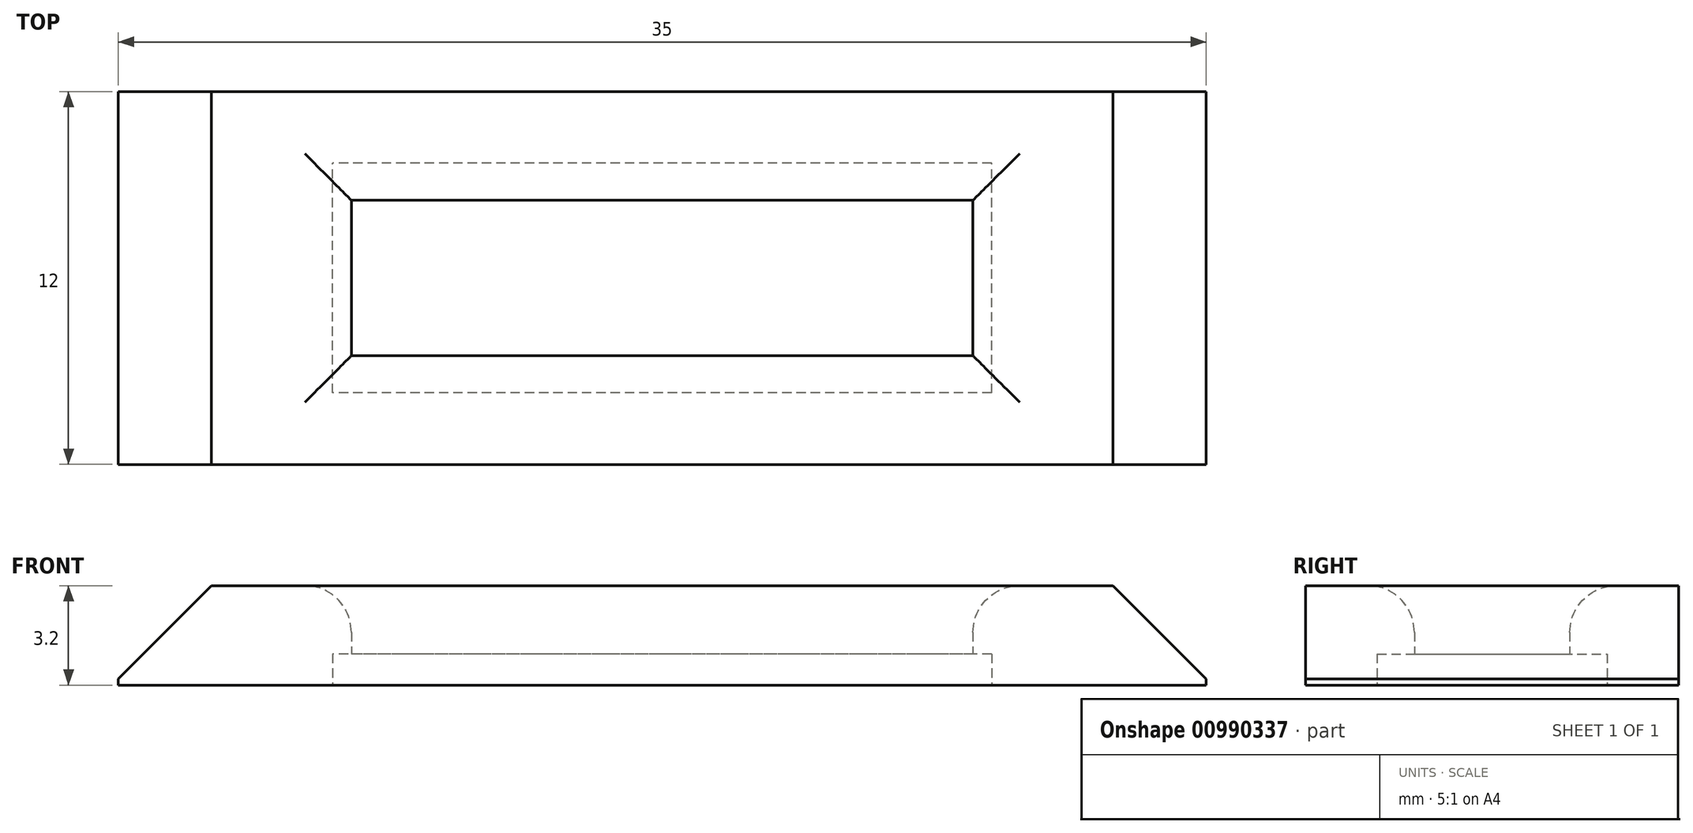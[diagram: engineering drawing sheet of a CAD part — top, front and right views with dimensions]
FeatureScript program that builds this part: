
annotation { "Feature Type Name" : "Feature", "Feature Type Description" : "" }
export const myFeature = defineFeature(function(context is Context, id is Id, definition is map)
    precondition{}
    {
        {
            var Q0;
            Q0=qCreatedBy(makeId("Top.planeOp"),FACE);
            var sketch = newSketch(context, id + "F0", { "sketchPlane" : qUnion([Q0])});
            skLineSegment(sketch, "E0.bottom", {"start": v(-51.31, 31.06) * mm, "end": v(-31.31, 31.06) * mm});
            skLineSegment(sketch, "E0.left", {"start": v(-51.31, 31.06) * mm, "end": v(-51.31, 26.06) * mm});
            skLineSegment(sketch, "E0.right", {"start": v(-31.31, 31.06) * mm, "end": v(-31.31, 26.06) * mm});
            skLineSegment(sketch, "E1.bottom", {"start": v(-58.81, 34.56) * mm, "end": v(-23.81, 34.56) * mm});
            skLineSegment(sketch, "E1.left", {"start": v(-58.81, 34.56) * mm, "end": v(-58.81, 22.56) * mm});
            skLineSegment(sketch, "E1.right", {"start": v(-23.81, 34.56) * mm, "end": v(-23.81, 22.56) * mm});
            skPoint(sketch, "E1.middle", {"position": v(-41.31, 28.56) * mm});
            skPoint(sketch, "E1.middle.positionSnap0", {"position": v(-51.31, 28.56) * mm});
            skPoint(sketch, "E1.middle.positionSnap1", {"position": v(-41.31, 31.06) * mm});
            skPoint(sketch, "E1.centerSnap0", {"position": v(-51.31, 28.56) * mm});
            skPoint(sketch, "E1.centerSnap1", {"position": v(-41.31, 31.06) * mm});
            skLineSegment(sketch, "E2", {"start": v(-58.81, 22.56) * mm, "end": v(-23.81, 22.56) * mm});
            skLineSegment(sketch, "E3", {"start": v(-31.31, 26.06) * mm, "end": v(-51.31, 26.06) * mm});
            skSolve(sketch);
        }
        {
            var Q0;
            Q0=makeQuery(id+"F0.imprint","IMPRINT",FACE,{"disambiguationData":[TD([[makeQuery(id+"F0.imprint","IMPRINT",EDGE,{"derivedFrom":sQuery(id+"F0.wireOp",EDGE,"E0.bottom")}),1.0]])]});
            extrude(context, id + "F1", {"entities" : qUnion([Q0]), "depth" : 3.2 * mm, "offsetDistance" : 25 * mm});
        }
        {
            var Q0;
            Q0=makeQuery(id+"F1.opExtrude","CAP_EDGE",EDGE,{"disambiguationData":[OSD([sQuery(id+"F0.wireOp",EDGE,"E0.bottom")])],"isStart":false});
            var Q1;
            Q1=makeQuery(id+"F1.opExtrude","CAP_EDGE",EDGE,{"disambiguationData":[OSD([sQuery(id+"F0.wireOp",EDGE,"E0.right")])],"isStart":false});
            var Q2;
            Q2=makeQuery(id+"F1.opExtrude","CAP_EDGE",EDGE,{"disambiguationData":[OSD([sQuery(id+"F0.wireOp",EDGE,"E0.left")])],"isStart":false});
            var Q3;
            Q3=makeQuery(id+"F1.opExtrude","CAP_EDGE",EDGE,{"disambiguationData":[OSD([sQuery(id+"F0.wireOp",EDGE,"E3")])],"isStart":false});
            fillet(context, id + "F2", {"entities" : qUnion([Q0, Q1, Q2, Q3]), "radius" : 1.5 * mm, "tangentPropagation" : true, "allowEdgeOverflow" : false});
        }
        {
            var Q0;
            Q0=makeQuery(id+"F1.opExtrude","CAP_FACE",FACE,{"disambiguationData":[OSD([sQuery(id+"F0.wireOp",EDGE,"E0.bottom"),sQuery(id+"F0.wireOp",EDGE,"E0.left"),sQuery(id+"F0.wireOp",EDGE,"E0.right"),sQuery(id+"F0.wireOp",EDGE,"E1.bottom"),sQuery(id+"F0.wireOp",EDGE,"E1.left"),sQuery(id+"F0.wireOp",EDGE,"E1.right"),sQuery(id+"F0.wireOp",EDGE,"3cnDEh5t-rJ0t-s9qo-ouWh-H4Ytwz6xX1wR"),sQuery(id+"F0.wireOp",EDGE,"w3A0wrpz-weP8-O1Qo-NG7g-3hIWCTH4h6xS")])],"isStart":true});
            var sketch = newSketch(context, id + "F3", { "sketchPlane" : qUnion([Q0])});
            skLineSegment(sketch, "E4.bottom", {"start": v(-30.71, -24.86) * mm, "end": v(-51.91, -24.86) * mm});
            skLineSegment(sketch, "E4.top", {"start": v(-30.71, -32.26) * mm, "end": v(-51.91, -32.26) * mm});
            skLineSegment(sketch, "E4.left", {"start": v(-30.71, -24.86) * mm, "end": v(-30.71, -32.26) * mm});
            skLineSegment(sketch, "E4.right", {"start": v(-51.91, -24.86) * mm, "end": v(-51.91, -32.26) * mm});
            skPoint(sketch, "E4.middle", {"position": v(-41.31, -28.56) * mm});
            skPoint(sketch, "E4.middle.positionSnap0", {"position": v(-31.31, -28.56) * mm});
            skPoint(sketch, "E4.middle.positionSnap1", {"position": v(-41.31, -31.06) * mm});
            skPoint(sketch, "E4.centerSnap0", {"position": v(-31.31, -28.56) * mm});
            skPoint(sketch, "E4.centerSnap1", {"position": v(-41.31, -31.06) * mm});
            skSolve(sketch);
        }
        {
            var Q0;
            Q0 = qSketchRegion(id + "F3", true);
            extrude(context, id + "F4", {"entities" : qUnion([Q0]), "operationType" : NewBodyOperationType.REMOVE, "oppositeDirection" : true, "depth" : 1 * mm, "offsetDistance" : 25 * mm});
        }
        {
            var Q0;
            Q0=makeQuery(id+"F1.opExtrude","CAP_EDGE",EDGE,{"disambiguationData":[OSD([sQuery(id+"F0.wireOp",EDGE,"E1.left")])],"isStart":false});
            var Q1;
            Q1=makeQuery(id+"F1.opExtrude","CAP_EDGE",EDGE,{"disambiguationData":[OSD([sQuery(id+"F0.wireOp",EDGE,"E1.right")])],"isStart":false});
            chamfer(context, id + "F5", {"entities" : qUnion([Q0, Q1]), "chamferType" : ChamferType.TWO_OFFSETS, "width1" : 3 * mm, "oppositeDirection" : false, "width2" : 3 * mm, "tangentPropagation" : true});
        }
    });
